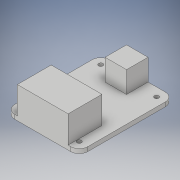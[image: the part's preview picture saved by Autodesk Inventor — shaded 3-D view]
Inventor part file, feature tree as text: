
AUTODESK INVENTOR PART (.ipt)
format: ipt  version: 2019 (Build 230136000, 136)  size: 143,872 bytes
history: native  units: in
note: dims shown in document units (in); Inventor stores cm internally (conversion verified against a paired STEP export)
features: extrude x3, sketch x3
ambient origin geometry x8: Origin, YZ Plane, XZ Plane, XY Plane, X Axis, Y Axis, Z Axis, Center Point
bodies: Solid1 (feature_tree)
feature tree (6):
  extrude  "Extrusion1"  Depth=1.1in
  extrude  "Extrusion2"  Depth=0.05in
  extrude  "Extrusion3"  Depth=0.05in
  sketch  "Sketch1"  dims[d0=0.85in d1=1.1in]
  sketch  "Sketch2"  dims[d2=0.1in d3=0.05in]
  sketch  "Sketch3"  dims[d4=0.05in d5=0.05in d6=0.05in d7=0.05in d8=0.0in d9=0.25in d10=0.25in d11=0.125in d12=0.25in d13=0.0in d14=0.5906in d15=0.3937in d16=0.315in d17=0.0in]
